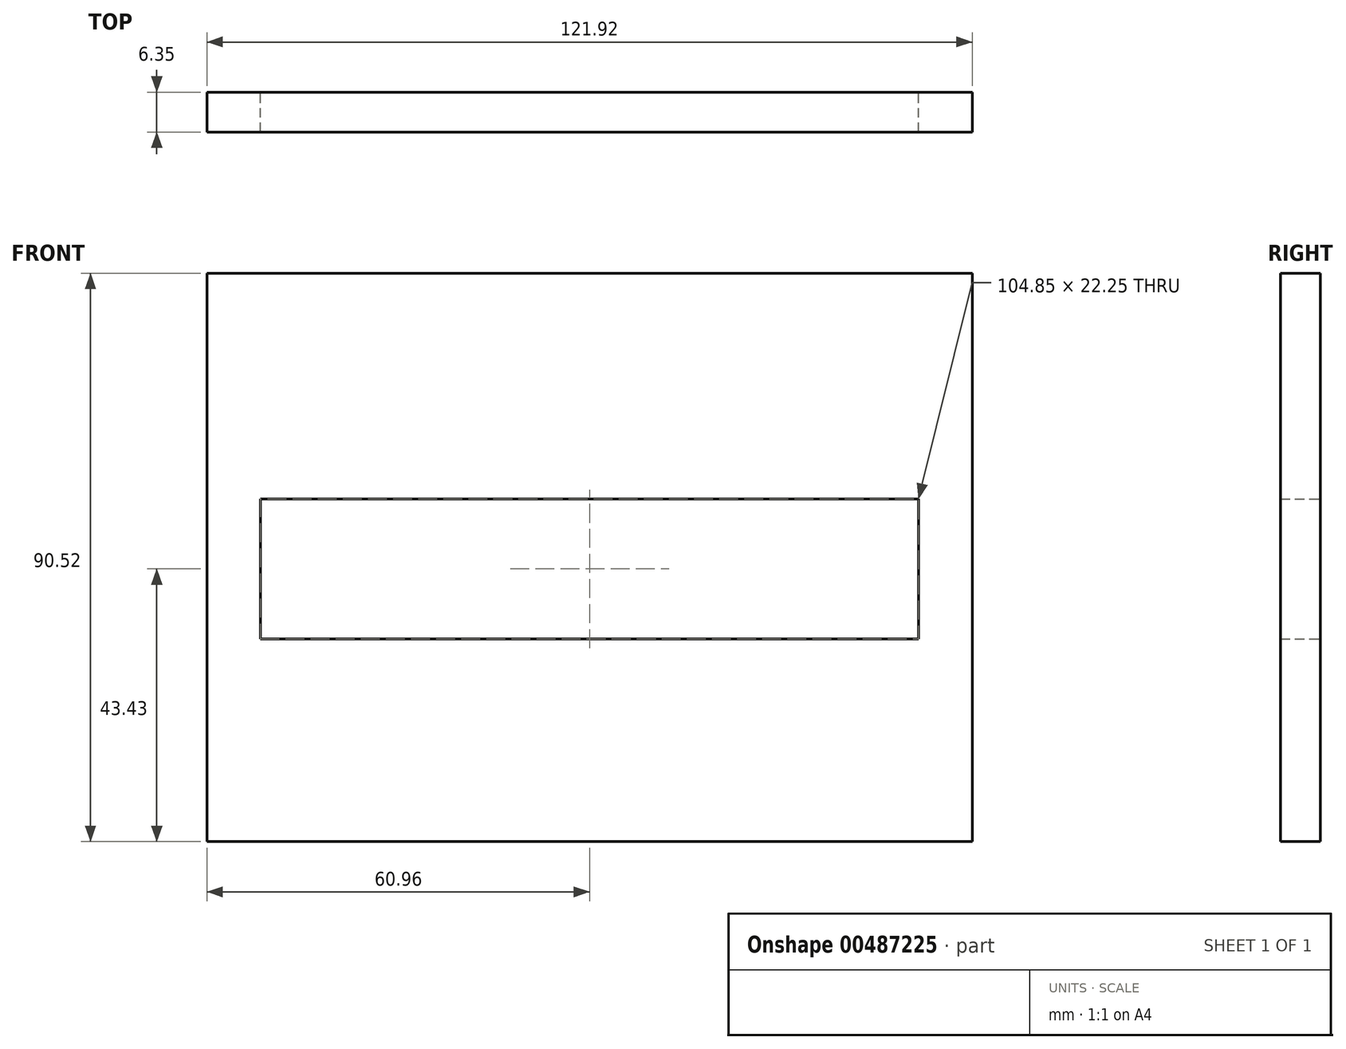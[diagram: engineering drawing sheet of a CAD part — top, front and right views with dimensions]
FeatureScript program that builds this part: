
annotation { "Feature Type Name" : "Feature", "Feature Type Description" : "" }
export const myFeature = defineFeature(function(context is Context, id is Id, definition is map)
    precondition{}
    {
        {
            var Q0;
            Q0=qCreatedBy(makeId("Front.planeOp"),FACE);
            var sketch = newSketch(context, id + "F0", { "sketchPlane" : qUnion([Q0])});
            skLineSegment(sketch, "E0.bottom", {"start": v(-60.96, 46.48) * mm, "end": v(60.96, 46.48) * mm});
            skLineSegment(sketch, "E0.top", {"start": v(-60.96, 10.52) * mm, "end": v(60.96, 10.52) * mm});
            skLineSegment(sketch, "E0.left", {"start": v(-60.96, 46.48) * mm, "end": v(-60.96, 10.52) * mm});
            skLineSegment(sketch, "E0.right", {"start": v(60.96, 46.48) * mm, "end": v(60.96, 10.52) * mm});
            skPoint(sketch, "E0.middle", {"position": v(0, 28.5) * mm});
            skLineSegment(sketch, "E1.bottom", {"start": v(-60.96, -11.73) * mm, "end": v(60.96, -11.73) * mm});
            skLineSegment(sketch, "E1.top", {"start": v(-60.96, -44.04) * mm, "end": v(60.96, -44.04) * mm});
            skLineSegment(sketch, "E1.left", {"start": v(-60.96, -11.73) * mm, "end": v(-60.96, -44.04) * mm});
            skLineSegment(sketch, "E1.right", {"start": v(60.96, -11.73) * mm, "end": v(60.96, -44.04) * mm});
            skPoint(sketch, "E1.middle", {"position": v(0, -27.89) * mm});
            skLineSegment(sketch, "E2.bottom", {"start": v(-60.96, 10.52) * mm, "end": v(-52.43, 10.52) * mm});
            skLineSegment(sketch, "E2.top", {"start": v(-60.96, -11.73) * mm, "end": v(-52.43, -11.73) * mm});
            skLineSegment(sketch, "E2.left", {"start": v(-60.96, 10.52) * mm, "end": v(-60.96, -11.73) * mm});
            skLineSegment(sketch, "E2.right", {"start": v(-52.43, 10.52) * mm, "end": v(-52.43, -11.73) * mm});
            skLineSegment(sketch, "E3.bottom", {"start": v(60.96, 10.52) * mm, "end": v(52.43, 10.52) * mm});
            skLineSegment(sketch, "E3.top", {"start": v(60.96, -11.73) * mm, "end": v(52.43, -11.73) * mm});
            skLineSegment(sketch, "E3.left", {"start": v(60.96, 10.52) * mm, "end": v(60.96, -11.73) * mm});
            skLineSegment(sketch, "E3.right", {"start": v(52.43, 10.52) * mm, "end": v(52.43, -11.73) * mm});
            skSolve(sketch);
        }
        {
            var Q0;
            Q0 = qSketchRegion(id + "F0", true);
            extrude(context, id + "F1", {"entities" : qUnion([Q0]), "depth" : 6.35 * mm});
        }
    });
